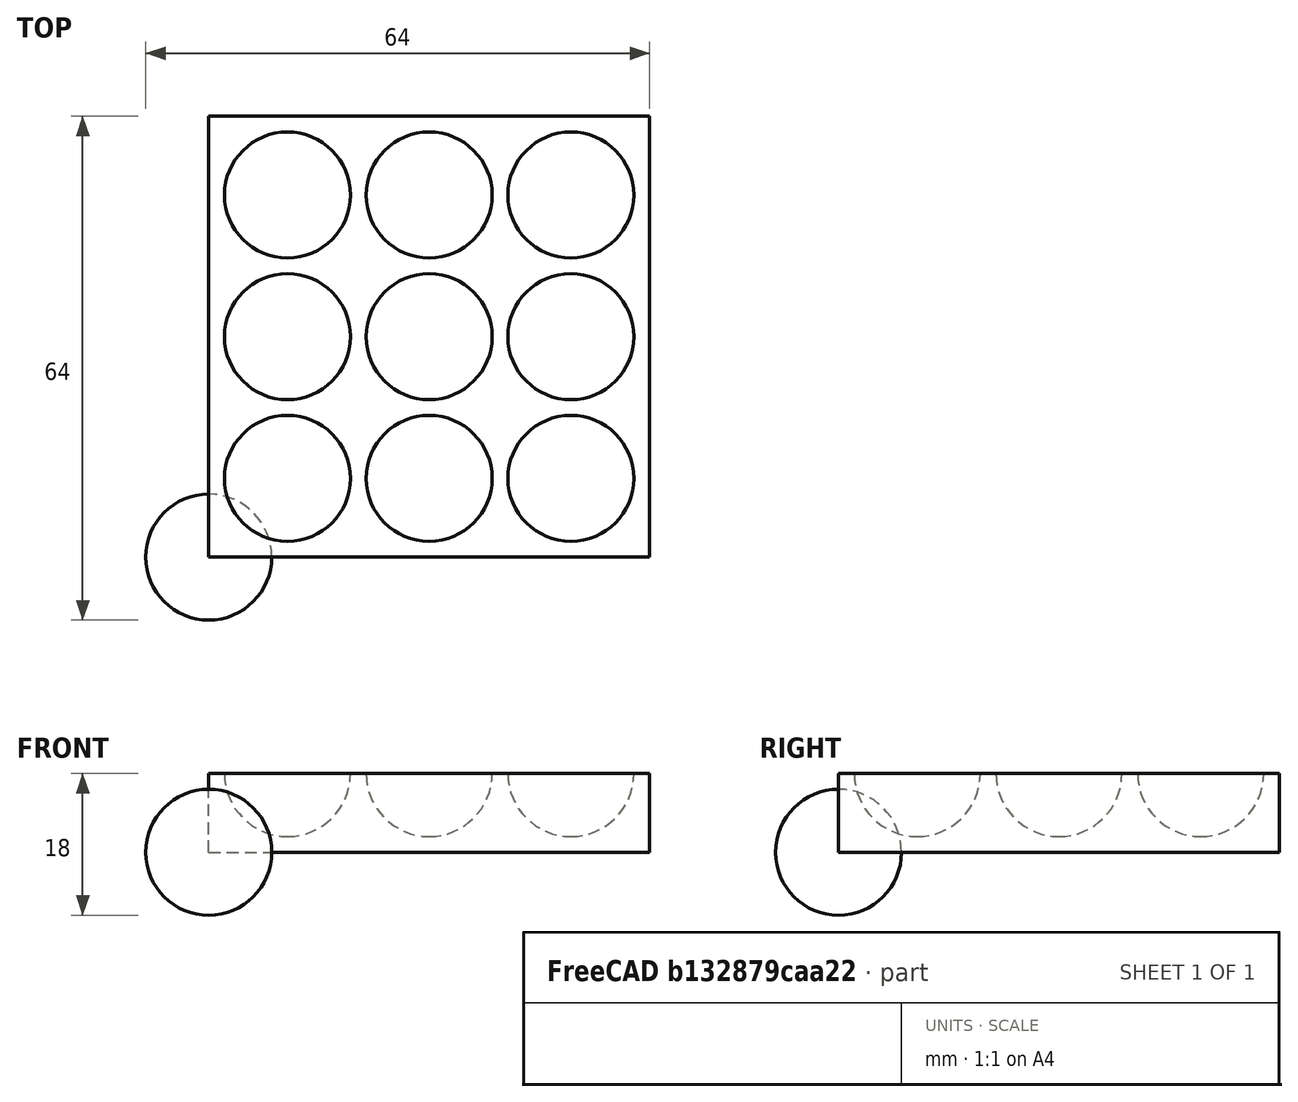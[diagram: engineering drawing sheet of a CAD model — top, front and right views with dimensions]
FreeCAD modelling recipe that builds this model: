
FCSTD DOCUMENT  (FreeCAD 1.0R39319 (Git))
Label: ojt1_t13r01_spheres
License: All rights reserved
LicenseURL: https://en.wikipedia.org/wiki/All_rights_reserved
objects: Part::Sphere×1, Part::FeaturePython×1, Part::Box×1, Part::Cut×1
note: 3 computed .brp shape members not serialized (recipe doc carries the construction recipe); baked Part::Feature solids carry a one-line shape summary decoded from their .brp

FEATURE [Part::Sphere] Sphere  label="Esfera"
  Angle1 = -90
  Angle2 = 90
  Angle3 = 360
  AttacherType = Attacher::AttachEngine3D
  Radius = 8
FEATURE [Part::FeaturePython] Array  # Draft array (typed FeaturePython)
  AlwaysSyncPlacement = false
  Angle = 360
  ArrayType = 0
  Axis = (0,0,1)
  Base = -> Sphere
  Center = (0,0,0)
  Count = 9
  ExpandArray = false
  Fuse = false
  IntervalAxis = (0,0,0)
  IntervalX = (18,0,0)
  IntervalY = (0,18,0)
  IntervalZ = (0,0,100)
  NumberCircles = 3
  NumberPolar = 5
  NumberX = 3
  NumberY = 3
  NumberZ = 1
  Placement = pos=(10,10,10) rot=(0,0,1;0rad)
  PlacementList = 9 placements: [(0,0,0),(0,18,0),(0,36,0),(18,0,0),(18,18,0),(18,36,0),(36,0,0),(36,18,0),(36,36,0)]
  RadialDistance = 50
  ScaleList = (9) [(1,1,1),(1,1,1),(1,1,1),(1,1,1),(1,1,1),(1,1,1),(1,1,1),(1,1,1),(1,1,1)]
  Symmetry = 1
  TangentialDistance = 25
FEATURE [Part::Box] Box  label="Cub"
  AttacherType = Attacher::AttachEngine3D
  Height = 10
  Length = 56
  Width = 56
FEATURE [Part::Cut] Cut
  Base = -> Box
  Refine = true
  Tool = -> Array
